# Revit family: Electrical_&_Lighting-Teknion-CQATL_Routes_Table_Lamp-R2018
name_source: partatom
category: Lighting Fixtures
revit_build: Autodesk Revit 2018 (Build: 20190510_1515(x64)
units: mm (PartAtom-declared; Revit-internal decimal feet)

## family parameters
Always vertical = Yes
Cut with Voids When Loaded = No
Light Source = Yes
OmniClass Number = 23.40.70.14.64.21
OmniClass Title = Systems Furniture
Part Type = Normal
Room Calculation Point = No
Round Connector Dimension = Use Diameter
Shared = Yes
Work Plane-Based = Yes

## types (1)
- Freestanding
    Apparent Load = 21 VA
    Assembly Code = E2020200
    Color Filter = 16777215
    Default Elevation = 48 "
    Description = Routes Table Lamp, Freestanding
    Dimming Lamp Color Temperature Shift = <None>
    Emit Shape Visible in Rendering = No
    Emit from Circle Diameter = 9 "
    Light Source Symbol Length = 10 "
    Manufacturer = Teknion
    Manufacturer Fax = 416.661.4586
    Model = CQATL1
    Part Number = CQATL
    Product Documentation Link = https://assets.teknion.com
    Product Line = Routes
    Product Page URL = https://www.teknion.com
    Series = Routes
    Spot Beam Angle = 45.00°
    Spot Field Angle = 60.00°
    Sustainability Data = http://www.teknion.com
    Tilt Angle = 90.00°
    URL = www.teknion.com
    Warranty = http://www.teknion.com

## geometry (parser evidence)
native form markers: Blend x2, Sweep x2
no freeform markers — native parametric forms only
